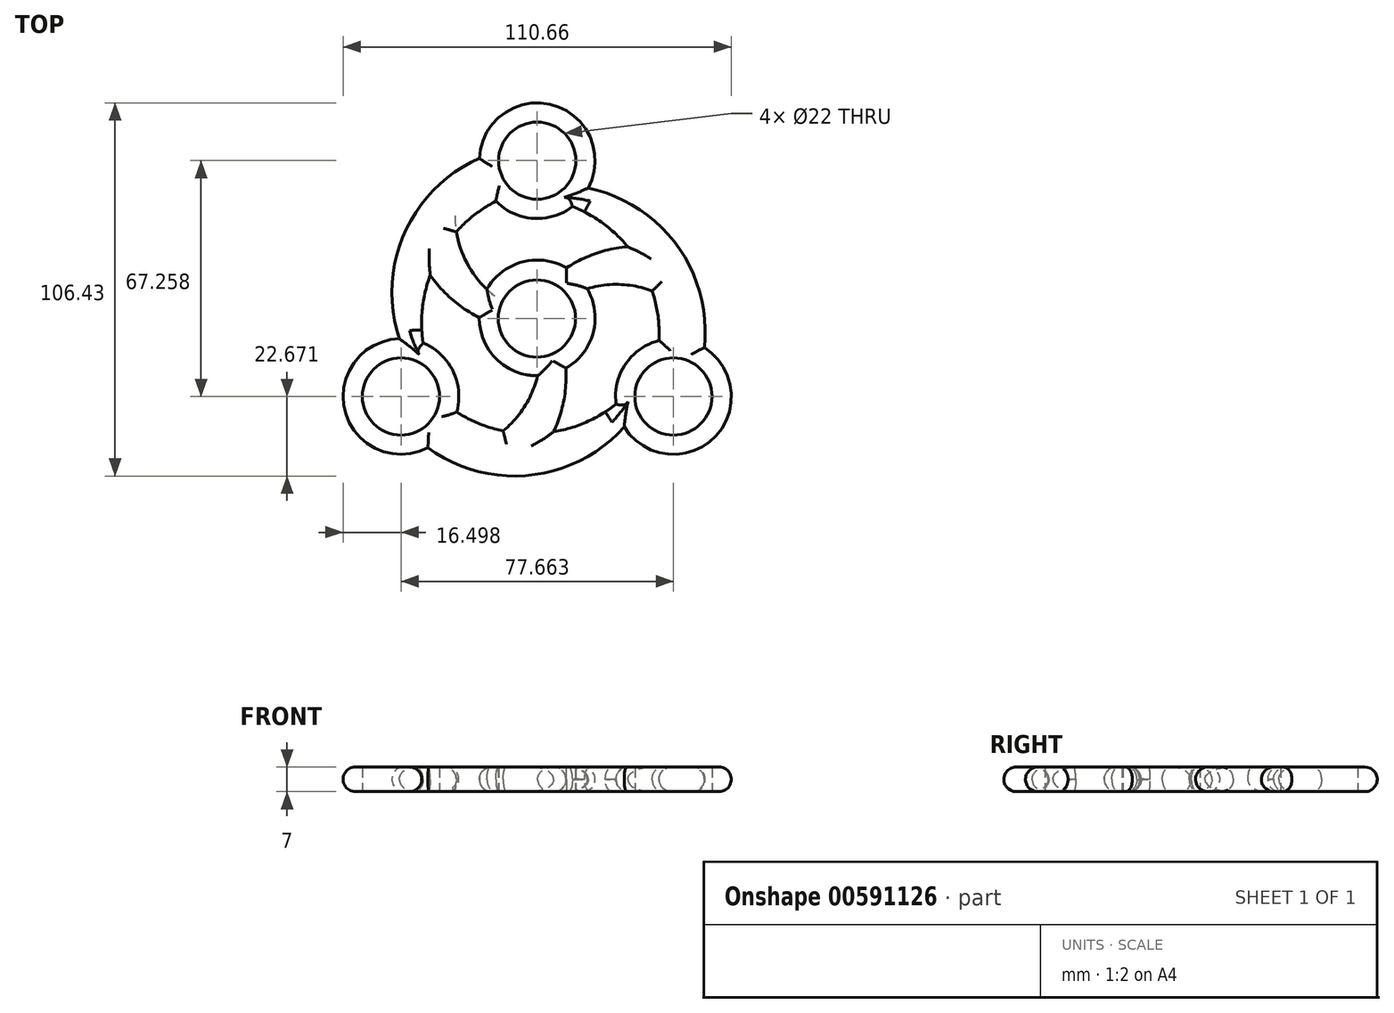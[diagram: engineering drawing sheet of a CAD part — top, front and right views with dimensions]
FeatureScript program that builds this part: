
annotation { "Feature Type Name" : "Feature", "Feature Type Description" : "" }
export const myFeature = defineFeature(function(context is Context, id is Id, definition is map)
    precondition{}
    {
        {
            var Q0;
            Q0=qCreatedBy(makeId("Top.planeOp"),FACE);
            var sketch = newSketch(context, id + "F0", { "sketchPlane" : qUnion([Q0])});
            skArc(sketch, "E0", {"start": v(8.19, -14.33) * mm, "mid": v(15.94, -4.26) * mm, "end": v(14.24, 8.33) * mm});
            skArc(sketch, "E1", {"start": v(14.54, 37.03) * mm, "mid": v(4.34, 60.76) * mm, "end": v(-16.49, 45.5) * mm});
            skCircle(sketch, "E2", {"center": v(0, 44.84) * mm, "radius": 11 * mm});
            skCircle(sketch, "E3", {"center": v(-0.1, -0.18) * mm, "radius": 11 * mm});
            skArc(sketch, "E4", {"start": v(34.72, -6.44) * mm, "mid": v(34.4, 0.73) * mm, "end": v(32.77, 7.71) * mm});
            skArc(sketch, "E5", {"start": v(14.54, 37.03) * mm, "mid": v(39.86, 20.66) * mm, "end": v(47.64, -8.47) * mm});
            skArc(sketch, "E6", {"start": v(8.31, 14.25) * mm, "mid": v(16.68, 18.36) * mm, "end": v(25.8, 20.3) * mm});
            skArc(sketch, "E7", {"start": v(32.77, 7.71) * mm, "mid": v(23.56, 9.54) * mm, "end": v(14.24, 8.33) * mm});
            skArc(sketch, "E8.trimOffspring", {"start": v(25.8, 20.3) * mm, "mid": v(18.66, 27.03) * mm, "end": v(10.06, 31.76) * mm});
            skArc(sketch, "E9.1.0", {"start": v(-23.06, 24.52) * mm, "mid": v(-20.04, 15.63) * mm, "end": v(-14.34, 8.17) * mm});
            skCircle(sketch, "E9.1.1", {"center": v(-38.83, -22.42) * mm, "radius": 11 * mm});
            skArc(sketch, "E9.1.2", {"start": v(-11.78, 33.29) * mm, "mid": v(-17.83, 29.42) * mm, "end": v(-23.06, 24.52) * mm});
            skArc(sketch, "E9.1.3", {"start": v(-30.49, 12.2) * mm, "mid": v(-32.74, 2.64) * mm, "end": v(-32.54, -7.17) * mm});
            skArc(sketch, "E9.1.4", {"start": v(-39.34, -5.93) * mm, "mid": v(-37.83, 24.2) * mm, "end": v(-16.49, 45.5) * mm});
            skArc(sketch, "E9.1.5", {"start": v(-39.34, -5.93) * mm, "mid": v(-54.79, -26.62) * mm, "end": v(-31.16, -37.03) * mm});
            skArc(sketch, "E9.1.7", {"start": v(-16.5, 0.07) * mm, "mid": v(-24.24, 5.27) * mm, "end": v(-30.49, 12.2) * mm});
            skArc(sketch, "E9.2.0", {"start": v(-9.7, -32.24) * mm, "mid": v(-3.52, -25.17) * mm, "end": v(0.1, -16.5) * mm});
            skCircle(sketch, "E9.2.1", {"center": v(38.83, -22.42) * mm, "radius": 11 * mm});
            skArc(sketch, "E9.2.2", {"start": v(-22.94, -26.85) * mm, "mid": v(-16.57, -30.15) * mm, "end": v(-9.7, -32.24) * mm});
            skArc(sketch, "E9.2.3", {"start": v(4.68, -32.5) * mm, "mid": v(14.08, -29.67) * mm, "end": v(22.48, -24.6) * mm});
            skArc(sketch, "E9.2.4", {"start": v(24.8, -31.1) * mm, "mid": v(-2.04, -44.85) * mm, "end": v(-31.16, -37.03) * mm});
            skArc(sketch, "E9.2.5", {"start": v(24.8, -31.1) * mm, "mid": v(50.45, -34.14) * mm, "end": v(47.64, -8.47) * mm});
            skArc(sketch, "E9.2.7", {"start": v(8.19, -14.33) * mm, "mid": v(7.56, -23.63) * mm, "end": v(4.68, -32.5) * mm});
            skArc(sketch, "E10.trimOffspring", {"start": v(-16.5, 0.07) * mm, "mid": v(-11.66, -11.67) * mm, "end": v(0.1, -16.5) * mm});
            skArc(sketch, "E11.trimOffspring", {"start": v(8.31, 14.25) * mm, "mid": v(-4.28, 15.94) * mm, "end": v(-14.34, 8.17) * mm});
            skArc(sketch, "E12.trimOffspring", {"start": v(-22.94, -26.85) * mm, "mid": v(-24, -15.18) * mm, "end": v(-32.54, -7.17) * mm});
            skArc(sketch, "E13.trimOffspring", {"start": v(34.72, -6.44) * mm, "mid": v(25.15, -13.2) * mm, "end": v(22.48, -24.6) * mm});
            skArc(sketch, "E14.trimOffspring", {"start": v(-11.78, 33.29) * mm, "mid": v(-1.15, 28.38) * mm, "end": v(10.06, 31.76) * mm});
            skSolve(sketch);
        }
        {
            var Q0;
            Q0=makeQuery(id+"F0.imprint","IMPRINT",FACE,{"disambiguationData":[TD([[makeQuery(id+"F0.imprint","IMPRINT",EDGE,{"derivedFrom":sQuery(id+"F0.wireOp",EDGE,"E0")}),1.0]])]});
            extrude(context, id + "F1", {"entities" : qUnion([Q0]), "depth" : 7 * mm, "offsetDistance" : 25 * mm});
        }
        {
            var Q0;
            Q0=makeQuery(id+"F1.opExtrude","CAP_EDGE",EDGE,{"disambiguationData":[OSD([sQuery(id+"F0.wireOp",EDGE,"E5")])],"isStart":false});
            var Q1;
            Q1=makeQuery(id+"F1.opExtrude","CAP_EDGE",EDGE,{"disambiguationData":[OSD([sQuery(id+"F0.wireOp",EDGE,"E9.2.5")])],"isStart":false});
            var Q2;
            Q2=makeQuery(id+"F1.opExtrude","CAP_EDGE",EDGE,{"disambiguationData":[OSD([sQuery(id+"F0.wireOp",EDGE,"E9.2.5")])],"isStart":true});
            var Q3;
            Q3=makeQuery(id+"F1.opExtrude","CAP_EDGE",EDGE,{"disambiguationData":[OSD([sQuery(id+"F0.wireOp",EDGE,"E5")])],"isStart":true});
            fillet(context, id + "F2", {"entities" : qUnion([Q0, Q1, Q2, Q3]), "radius" : 3.5 * mm, "tangentPropagation" : true, "allowEdgeOverflow" : false});
        }
        {
            var Q0;
            Q0=makeQuery(id+"F1.opExtrude","CAP_EDGE",EDGE,{"disambiguationData":[OSD([sQuery(id+"F0.wireOp",EDGE,"E1")])],"isStart":false});
            var Q1;
            Q1=makeQuery(id+"F1.opExtrude","CAP_EDGE",EDGE,{"disambiguationData":[OSD([sQuery(id+"F0.wireOp",EDGE,"E1")])],"isStart":true});
            var Q2;
            Q2=makeQuery(id+"F1.opExtrude","CAP_EDGE",EDGE,{"disambiguationData":[OSD([sQuery(id+"F0.wireOp",EDGE,"E9.1.4")])],"isStart":false});
            var Q3;
            Q3=makeQuery(id+"F1.opExtrude","CAP_EDGE",EDGE,{"disambiguationData":[OSD([sQuery(id+"F0.wireOp",EDGE,"E9.1.4")])],"isStart":true});
            fillet(context, id + "F3", {"entities" : qUnion([Q0, Q1, Q2, Q3]), "radius" : 3.5 * mm, "tangentPropagation" : true, "allowEdgeOverflow" : false});
        }
        {
            var Q0;
            Q0=makeQuery(id+"F1.opExtrude","CAP_EDGE",EDGE,{"disambiguationData":[OSD([sQuery(id+"F0.wireOp",EDGE,"E9.1.5")])],"isStart":true});
            var Q1;
            Q1=makeQuery(id+"F1.opExtrude","CAP_EDGE",EDGE,{"disambiguationData":[OSD([sQuery(id+"F0.wireOp",EDGE,"E9.1.5")])],"isStart":false});
            var Q2;
            Q2=makeQuery(id+"F1.opExtrude","CAP_EDGE",EDGE,{"disambiguationData":[OSD([sQuery(id+"F0.wireOp",EDGE,"E9.2.4")])],"isStart":true});
            var Q3;
            Q3=makeQuery(id+"F1.opExtrude","CAP_EDGE",EDGE,{"disambiguationData":[OSD([sQuery(id+"F0.wireOp",EDGE,"E9.2.4")])],"isStart":false});
            fillet(context, id + "F4", {"entities" : qUnion([Q0, Q1, Q2, Q3]), "radius" : 3.5 * mm, "tangentPropagation" : true, "allowEdgeOverflow" : false});
        }
        {
            var Q0;
            Q0=makeQuery(id+"F1.opExtrude","CAP_EDGE",EDGE,{"disambiguationData":[OSD([sQuery(id+"F0.wireOp",EDGE,"E12.trimOffspring")])],"isStart":false});
            var Q1;
            Q1=makeQuery(id+"F1.opExtrude","CAP_EDGE",EDGE,{"disambiguationData":[OSD([sQuery(id+"F0.wireOp",EDGE,"E12.trimOffspring")])],"isStart":true});
            var Q2;
            Q2=makeQuery(id+"F1.opExtrude","CAP_EDGE",EDGE,{"disambiguationData":[OSD([sQuery(id+"F0.wireOp",EDGE,"E9.2.2")])],"isStart":true});
            var Q3;
            Q3=makeQuery(id+"F1.opExtrude","CAP_EDGE",EDGE,{"disambiguationData":[OSD([sQuery(id+"F0.wireOp",EDGE,"E9.2.2")])],"isStart":false});
            var Q4;
            Q4=makeQuery(id+"F1.opExtrude","CAP_EDGE",EDGE,{"disambiguationData":[OSD([sQuery(id+"F0.wireOp",EDGE,"E9.1.3")])],"isStart":true});
            var Q5;
            Q5=makeQuery(id+"F1.opExtrude","CAP_EDGE",EDGE,{"disambiguationData":[OSD([sQuery(id+"F0.wireOp",EDGE,"E9.1.3")])],"isStart":false});
            var Q6;
            Q6=makeQuery(id+"F1.opExtrude","CAP_EDGE",EDGE,{"disambiguationData":[OSD([sQuery(id+"F0.wireOp",EDGE,"E9.1.7")])],"isStart":true});
            var Q7;
            Q7=makeQuery(id+"F1.opExtrude","CAP_EDGE",EDGE,{"disambiguationData":[OSD([sQuery(id+"F0.wireOp",EDGE,"E9.1.7")])],"isStart":false});
            var Q8;
            Q8=makeQuery(id+"F1.opExtrude","CAP_EDGE",EDGE,{"disambiguationData":[OSD([sQuery(id+"F0.wireOp",EDGE,"E10.trimOffspring")])],"isStart":true});
            var Q9;
            Q9=makeQuery(id+"F1.opExtrude","CAP_EDGE",EDGE,{"disambiguationData":[OSD([sQuery(id+"F0.wireOp",EDGE,"E10.trimOffspring")])],"isStart":false});
            var Q10;
            Q10=makeQuery(id+"F1.opExtrude","CAP_EDGE",EDGE,{"disambiguationData":[OSD([sQuery(id+"F0.wireOp",EDGE,"E9.2.0")])],"isStart":true});
            var Q11;
            Q11=makeQuery(id+"F1.opExtrude","CAP_EDGE",EDGE,{"disambiguationData":[OSD([sQuery(id+"F0.wireOp",EDGE,"E9.2.0")])],"isStart":false});
            fillet(context, id + "F5", {"entities" : qUnion([Q0, Q1, Q2, Q3, Q4, Q5, Q6, Q7, Q8, Q9, Q10, Q11]), "radius" : 3.5 * mm, "tangentPropagation" : true, "allowEdgeOverflow" : false});
        }
        {
            var Q0;
            Q0=makeQuery(id+"F1.opExtrude","CAP_EDGE",EDGE,{"disambiguationData":[OSD([sQuery(id+"F0.wireOp",EDGE,"E7")])],"isStart":false});
            var Q1;
            Q1=makeQuery(id+"F1.opExtrude","CAP_EDGE",EDGE,{"disambiguationData":[OSD([sQuery(id+"F0.wireOp",EDGE,"E0")])],"isStart":false});
            var Q2;
            Q2=makeQuery(id+"F1.opExtrude","CAP_EDGE",EDGE,{"disambiguationData":[OSD([sQuery(id+"F0.wireOp",EDGE,"E9.2.7")])],"isStart":false});
            var Q3;
            Q3=makeQuery(id+"F1.opExtrude","CAP_EDGE",EDGE,{"disambiguationData":[OSD([sQuery(id+"F0.wireOp",EDGE,"E9.2.3")])],"isStart":false});
            var Q4;
            Q4=makeQuery(id+"F1.opExtrude","CAP_EDGE",EDGE,{"disambiguationData":[OSD([sQuery(id+"F0.wireOp",EDGE,"E13.trimOffspring")])],"isStart":false});
            var Q5;
            Q5=makeQuery(id+"F1.opExtrude","CAP_EDGE",EDGE,{"disambiguationData":[OSD([sQuery(id+"F0.wireOp",EDGE,"E4")])],"isStart":false});
            var Q6;
            Q6=makeQuery(id+"F1.opExtrude","CAP_EDGE",EDGE,{"disambiguationData":[OSD([sQuery(id+"F0.wireOp",EDGE,"E9.1.0")])],"isStart":false});
            var Q7;
            Q7=makeQuery(id+"F1.opExtrude","CAP_EDGE",EDGE,{"disambiguationData":[OSD([sQuery(id+"F0.wireOp",EDGE,"E9.1.2")])],"isStart":false});
            var Q8;
            Q8=makeQuery(id+"F1.opExtrude","CAP_EDGE",EDGE,{"disambiguationData":[OSD([sQuery(id+"F0.wireOp",EDGE,"E14.trimOffspring")])],"isStart":false});
            var Q9;
            Q9=makeQuery(id+"F1.opExtrude","CAP_EDGE",EDGE,{"disambiguationData":[OSD([sQuery(id+"F0.wireOp",EDGE,"E11.trimOffspring")])],"isStart":false});
            var Q10;
            Q10=makeQuery(id+"F1.opExtrude","CAP_EDGE",EDGE,{"disambiguationData":[OSD([sQuery(id+"F0.wireOp",EDGE,"E6")])],"isStart":false});
            var Q11;
            Q11=makeQuery(id+"F1.opExtrude","CAP_EDGE",EDGE,{"disambiguationData":[OSD([sQuery(id+"F0.wireOp",EDGE,"E8.trimOffspring")])],"isStart":false});
            fillet(context, id + "F6", {"entities" : qUnion([Q0, Q1, Q2, Q3, Q4, Q5, Q6, Q7, Q8, Q9, Q10, Q11]), "radius" : 3.5 * mm, "tangentPropagation" : true, "allowEdgeOverflow" : false});
        }
        {
            var Q0;
            {var subQ0=sQuery(id+"F0.wireOp",EDGE,"E9.1.0");Q0=makeQuery(id+"F6.opFillet","BLEND_EDGE",EDGE,{"blendedFrom":[makeQuery(id+"F1.opExtrude","CAP_EDGE",EDGE,{"disambiguationData":[OSD([subQ0])],"isStart":false}),makeQuery(id+"F1.opExtrude","SWEPT_FACE",FACE,{"disambiguationData":[OSD([subQ0])]})],"blendedInto":[makeQuery(id+"F1.opExtrude","SWEPT_FACE",FACE,{"disambiguationData":[OSD([subQ0])]})]});}
            var Q1;
            Q1=makeQuery(id+"F1.opExtrude","CAP_EDGE",EDGE,{"disambiguationData":[OSD([sQuery(id+"F0.wireOp",EDGE,"E9.1.2")])],"isStart":true});
            var Q2;
            Q2=makeQuery(id+"F1.opExtrude","CAP_EDGE",EDGE,{"disambiguationData":[OSD([sQuery(id+"F0.wireOp",EDGE,"E11.trimOffspring")])],"isStart":true});
            var Q3;
            Q3=makeQuery(id+"F1.opExtrude","CAP_EDGE",EDGE,{"disambiguationData":[OSD([sQuery(id+"F0.wireOp",EDGE,"E14.trimOffspring")])],"isStart":true});
            var Q4;
            Q4=makeQuery(id+"F1.opExtrude","CAP_EDGE",EDGE,{"disambiguationData":[OSD([sQuery(id+"F0.wireOp",EDGE,"E8.trimOffspring")])],"isStart":true});
            var Q5;
            Q5=makeQuery(id+"F1.opExtrude","CAP_EDGE",EDGE,{"disambiguationData":[OSD([sQuery(id+"F0.wireOp",EDGE,"E6")])],"isStart":true});
            var Q6;
            Q6=makeQuery(id+"F1.opExtrude","CAP_EDGE",EDGE,{"disambiguationData":[OSD([sQuery(id+"F0.wireOp",EDGE,"E7")])],"isStart":true});
            var Q7;
            Q7=makeQuery(id+"F1.opExtrude","CAP_EDGE",EDGE,{"disambiguationData":[OSD([sQuery(id+"F0.wireOp",EDGE,"E0")])],"isStart":true});
            var Q8;
            Q8=makeQuery(id+"F1.opExtrude","CAP_EDGE",EDGE,{"disambiguationData":[OSD([sQuery(id+"F0.wireOp",EDGE,"E4")])],"isStart":true});
            var Q9;
            Q9=makeQuery(id+"F1.opExtrude","CAP_EDGE",EDGE,{"disambiguationData":[OSD([sQuery(id+"F0.wireOp",EDGE,"E13.trimOffspring")])],"isStart":true});
            var Q10;
            Q10=makeQuery(id+"F1.opExtrude","CAP_EDGE",EDGE,{"disambiguationData":[OSD([sQuery(id+"F0.wireOp",EDGE,"E9.2.7")])],"isStart":true});
            var Q11;
            Q11=makeQuery(id+"F1.opExtrude","CAP_EDGE",EDGE,{"disambiguationData":[OSD([sQuery(id+"F0.wireOp",EDGE,"E9.2.3")])],"isStart":true});
            fillet(context, id + "F7", {"entities" : qUnion([Q0, Q1, Q2, Q3, Q4, Q5, Q6, Q7, Q8, Q9, Q10, Q11]), "radius" : 3.5 * mm, "tangentPropagation" : true, "allowEdgeOverflow" : false});
        }
    });
